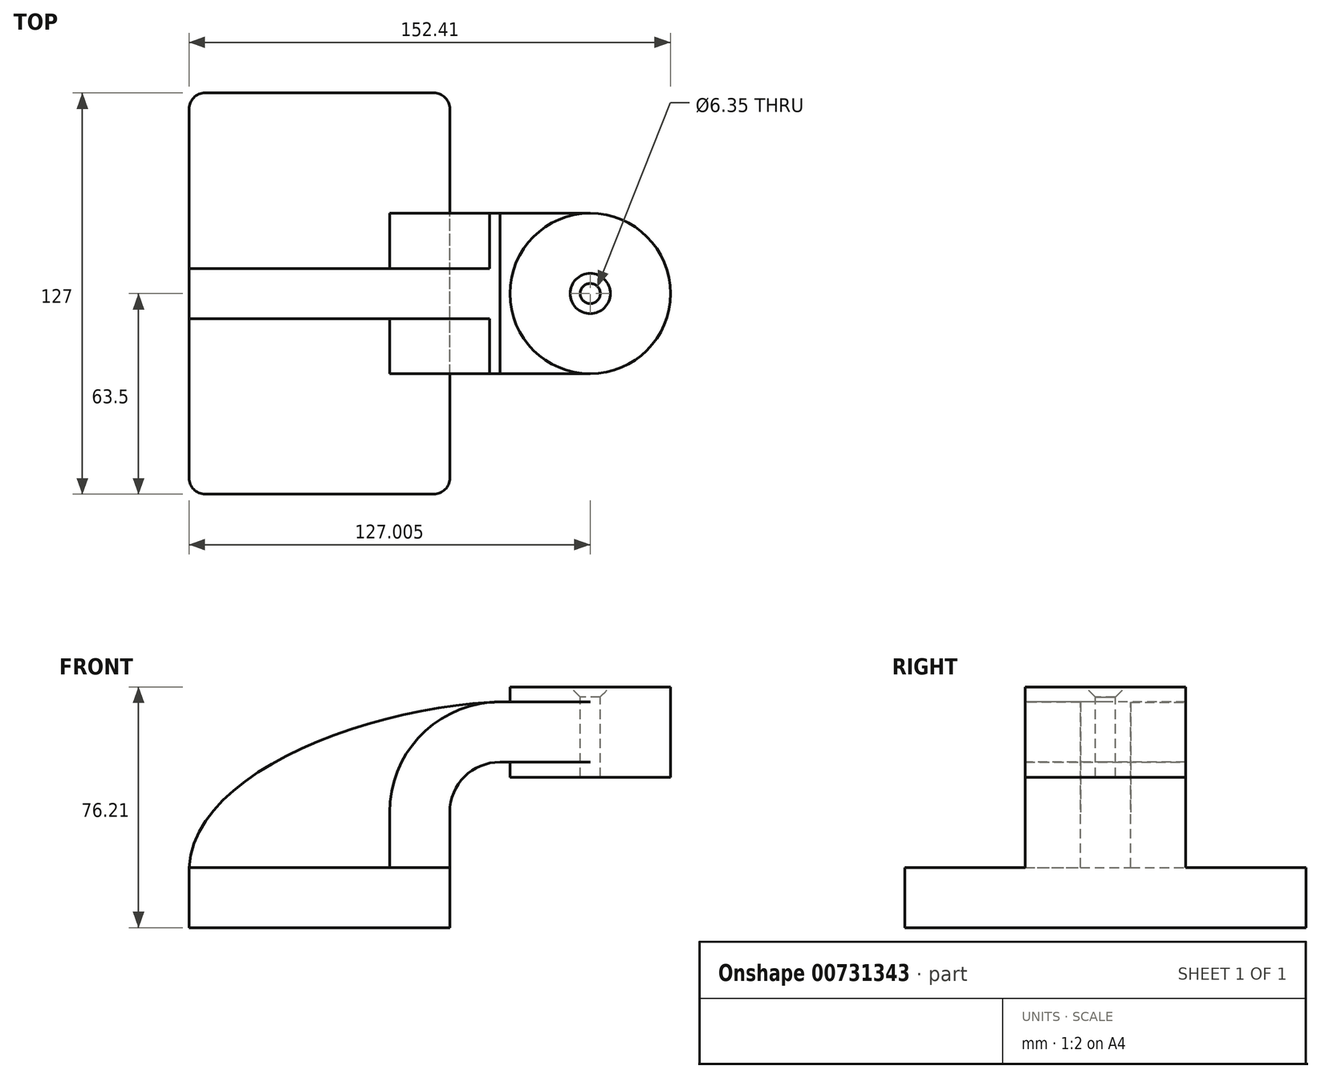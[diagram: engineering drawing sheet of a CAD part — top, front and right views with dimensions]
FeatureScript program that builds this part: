
annotation { "Feature Type Name" : "Feature", "Feature Type Description" : "" }
export const myFeature = defineFeature(function(context is Context, id is Id, definition is map)
    precondition{}
    {
        {
            var Q0;
            Q0=qCreatedBy(makeId("Front.planeOp"),FACE);
            var sketch = newSketch(context, id + "F0", { "sketchPlane" : qUnion([Q0])});
            skLineSegment(sketch, "E0.rect.bottom", {"start": v(-41.28, 9.52) * mm, "end": v(41.28, 9.52) * mm});
            skLineSegment(sketch, "E0.rect.top", {"start": v(-41.28, -9.52) * mm, "end": v(41.28, -9.52) * mm});
            skLineSegment(sketch, "E0.rect.left", {"start": v(-41.28, 9.52) * mm, "end": v(-41.28, -9.52) * mm});
            skLineSegment(sketch, "E0.rect.right", {"start": v(41.28, 9.52) * mm, "end": v(41.28, -9.52) * mm});
            skPoint(sketch, "E0.rect.middle", {"position": v(0, 0) * mm});
            skLineSegment(sketch, "E1", {"start": v(41.28, 9.52) * mm, "end": v(41.28, 27) * mm});
            skArc(sketch, "E2", {"start": v(41.28, 27) * mm, "mid": v(45.92, 38.23) * mm, "end": v(57.15, 42.88) * mm});
            skLineSegment(sketch, "E3", {"start": v(57.15, 42.88) * mm, "end": v(85.72, 42.88) * mm});
            skLineSegment(sketch, "E4.rect.bottom", {"start": v(60.32, 38.1) * mm, "end": v(111.12, 38.1) * mm});
            skLineSegment(sketch, "E4.rect.top", {"start": v(60.32, 66.68) * mm, "end": v(111.12, 66.68) * mm});
            skLineSegment(sketch, "E4.rect.left", {"start": v(60.32, 38.1) * mm, "end": v(60.32, 66.68) * mm});
            skLineSegment(sketch, "E4.rect.right", {"start": v(111.13, 38.1) * mm, "end": v(111.12, 66.68) * mm});
            skPoint(sketch, "E4.rect.middle", {"position": v(85.72, 52.39) * mm});
            skLineSegment(sketch, "E5.0", {"start": v(57.15, 61.93) * mm, "end": v(85.72, 61.93) * mm});
            skArc(sketch, "E5.1", {"start": v(22.23, 27) * mm, "mid": v(32.45, 51.7) * mm, "end": v(57.15, 61.93) * mm});
            skLineSegment(sketch, "E5.2", {"start": v(22.23, 9.52) * mm, "end": v(22.23, 27) * mm});
            skLineSegment(sketch, "E6", {"start": v(85.72, 38.1) * mm, "end": v(85.72, 66.68) * mm});
            skFitSpline(sketch, "E7", {"points": [v(-41.28, 9.53) * mm, v(57.15, 61.93) * mm], "startDerivative": vector(5.2, 92.34) * mm, "endDerivative": vector(120.92, 4.22) * mm});
            skSolve(sketch);
        }
        {
            var Q0;
            Q0=makeQuery(id+"F0.imprint","IMPRINT",FACE,{"disambiguationData":[TD([[makeQuery(id+"F0.imprint","IMPRINT",EDGE,{"derivedFrom":sQuery(id+"F0.wireOp",EDGE,"E0.rect.top")}),1.0]])]});
            extrude(context, id + "F1", {"entities" : qUnion([Q0]), "endBound" : BoundingType.SYMMETRIC, "depth" : 127 * mm});
        }
        {
            var Q0;
            {var subQ9=sQuery(id+"F0.wireOp",EDGE,"E1");Q0=makeQuery(id+"F0.imprint","IMPRINT",FACE,{"disambiguationData":[TD([[makeQuery(id+"F0.imprint","IMPRINT",EDGE,{"derivedFrom":subQ9}),1.0]])]});}
            var Q1;
            {var subQ0=sQuery(id+"F0.wireOp",EDGE,"E6");var subQ1=sQuery(id+"F0.wireOp",EDGE,"E3");var subQ2=makeQuery(id+"F0.imprint","INTERSECT",VERTEX,{"derivedFrom":[subQ1,subQ0]});Q1=makeQuery(id+"F0.imprint","IMPRINT",FACE,{"disambiguationData":[TD([[makeQuery(id+"F0.imprint","IMPRINT",EDGE,{"disambiguationData":[TD([[subQ2,1.0]])],"derivedFrom":subQ1}),1.0]])]});}
            extrude(context, id + "F2", {"entities" : qUnion([Q0, Q1]), "operationType" : NewBodyOperationType.ADD, "endBound" : BoundingType.SYMMETRIC, "depth" : 50.8 * mm});
        }
        {
            var Q0;
            {var subQ3=sQuery(id+"F0.wireOp",EDGE,"E5.2");Q0=makeQuery(id+"F0.imprint","IMPRINT",FACE,{"disambiguationData":[TD([[makeQuery(id+"F0.imprint","IMPRINT",EDGE,{"derivedFrom":subQ3}),1.0]])]});}
            extrude(context, id + "F3", {"entities" : qUnion([Q0]), "operationType" : NewBodyOperationType.ADD, "endBound" : BoundingType.SYMMETRIC, "depth" : 15.88 * mm});
        }
        {
            var Q0;
            {var subQ5=sQuery(id+"F0.wireOp",EDGE,"E4.rect.right");Q0=makeQuery(id+"F0.imprint","IMPRINT",FACE,{"disambiguationData":[TD([[makeQuery(id+"F0.imprint","IMPRINT",EDGE,{"derivedFrom":subQ5}),1.0]])]});}
            var Q1;
            Q1=sQuery(id+"F0.wireOp",EDGE,"E6");
            revolve(context, id + "F4", {"operationType" : NewBodyOperationType.ADD, "entities" : qUnion([Q0]), "axis" : qUnion([Q1]), "revolveType" : RevolveType.FULL});
        }
        {
            var Q0;
            Q0=makeQuery(id+"F1.opExtrude","CAP_EDGE",EDGE,{"disambiguationData":[OSD([sQuery(id+"F0.wireOp",EDGE,"E0.rect.right")])],"isStart":false});
            var Q1;
            Q1=makeQuery(id+"F1.opExtrude","CAP_EDGE",EDGE,{"disambiguationData":[OSD([sQuery(id+"F0.wireOp",EDGE,"E0.rect.left")])],"isStart":false});
            var Q2;
            Q2=makeQuery(id+"F1.opExtrude","CAP_EDGE",EDGE,{"disambiguationData":[OSD([sQuery(id+"F0.wireOp",EDGE,"E0.rect.right")])],"isStart":true});
            var Q3;
            Q3=makeQuery(id+"F1.opExtrude","CAP_EDGE",EDGE,{"disambiguationData":[OSD([sQuery(id+"F0.wireOp",EDGE,"E0.rect.left")])],"isStart":true});
            fillet(context, id + "F5", {"entities" : qUnion([Q0, Q1, Q2, Q3]), "radius" : 5.08 * mm, "tangentPropagation" : true, "allowEdgeOverflow" : false});
        }
        {
            var Q0;
            Q0=makeQuery(id+"F4.opRevolve","SWEPT_FACE",FACE,{"disambiguationData":[OSD([sQuery(id+"F0.wireOp",EDGE,"E4.rect.top")])]});
            var sketch = newSketch(context, id + "F6", { "sketchPlane" : qUnion([Q0])});
            skPoint(sketch, "E8", {"position": v(85.72, 0) * mm});
            skSolve(sketch);
        }
        {
            var Q0;
            Q0=sQuery(id+"F6.wireOp",VERTEX,"E8");
            var Q1;
            Q1=makeQuery(id+"F1.opExtrude","SWEPT_BODY",BODY,{"disambiguationData":[OSD([sQuery(id+"F0.wireOp",EDGE,"E0.rect.bottom"),sQuery(id+"F0.wireOp",EDGE,"E0.rect.top"),sQuery(id+"F0.wireOp",EDGE,"E0.rect.left"),sQuery(id+"F0.wireOp",EDGE,"E0.rect.right")])]});
            hole(context, id + "F7", {"style" : HoleStyle.C_SINK, "endStyle" : HoleEndStyle.THROUGH, "holeDiameter" : 6.35 * mm, "cSinkDiameter" : 12.7 * mm, "cSinkAngle" : 90 * degree, "majorDiameter" : 6.35 * mm, "isTappedThrough" : true, "tappedDepth" : 12.7 * mm, "tapClearance" : 3, "locations" : qUnion([Q0]), "scope" : qUnion([Q1])});
        }
    });
